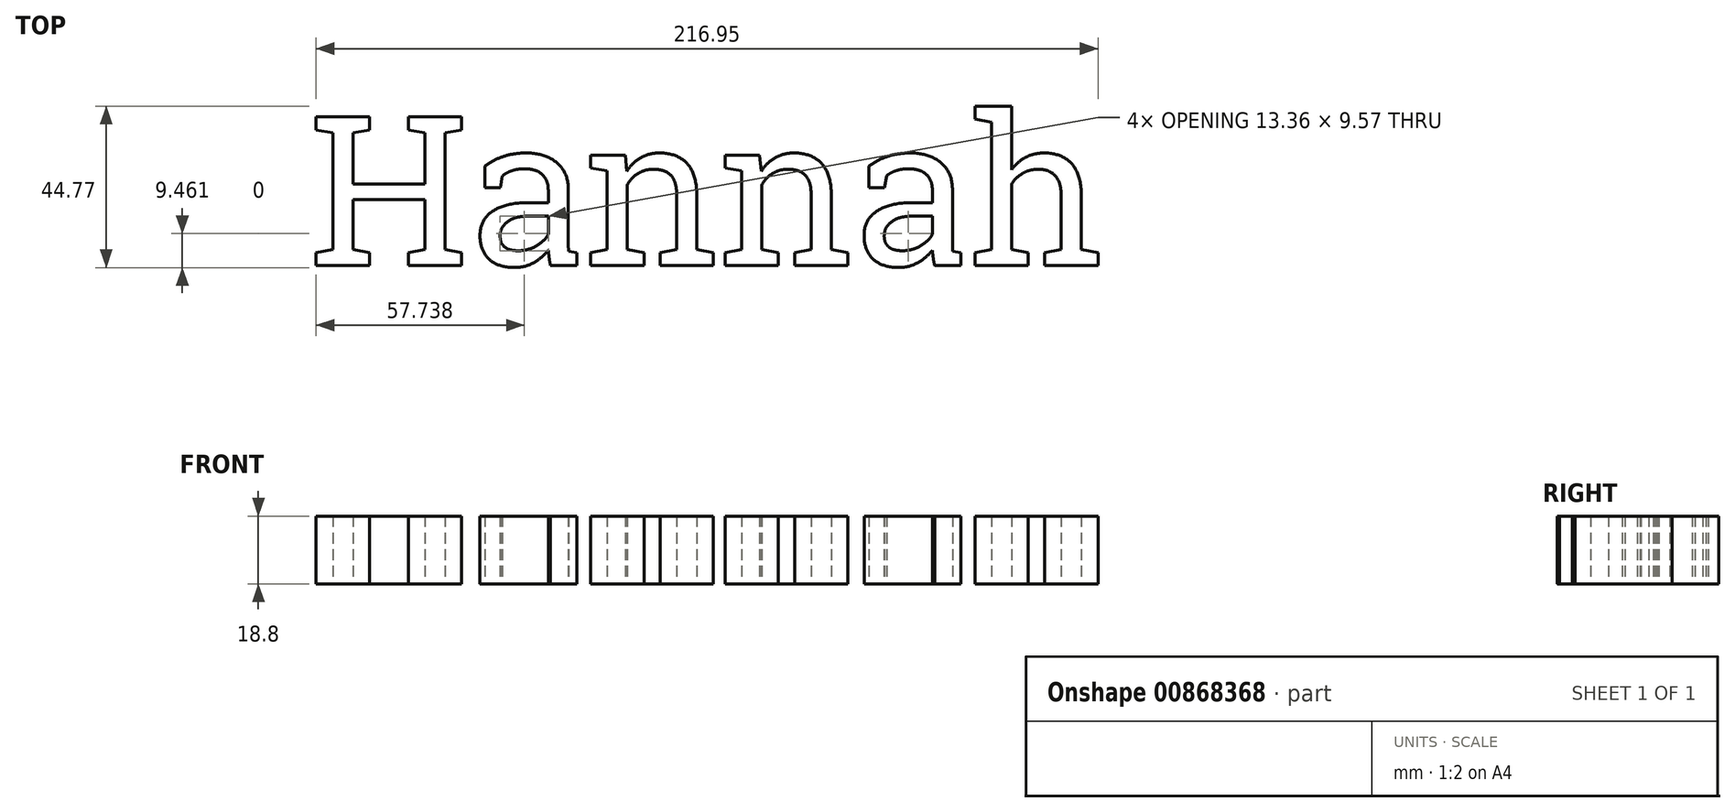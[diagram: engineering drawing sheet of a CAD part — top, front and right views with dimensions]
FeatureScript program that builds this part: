
annotation { "Feature Type Name" : "Feature", "Feature Type Description" : "" }
export const myFeature = defineFeature(function(context is Context, id is Id, definition is map)
    precondition{}
    {
        {
            var Q0;
            Q0=qCreatedBy(makeId("Top.planeOp"),FACE);
            var sketch = newSketch(context, id + "F0", { "sketchPlane" : qUnion([Q0])});
            skText(sketch, "E0", { "text": "Hannah", "fontName": "RobotoSlab-Regular.ttf"});
            const initialGuessF0  = {"E0": [-0.0606, 0.0025, 1, 0, 0.04175]};
            skSetInitialGuess(sketch, initialGuessF0);
            skSolve(sketch);
        }
        {
            var Q0;
            Q0 = qSketchRegion(id + "F0", true);
            extrude(context, id + "F1", {"entities" : qUnion([Q0]), "depth" : 18.8 * mm, "offsetDistance" : 25 * mm});
        }
    });
